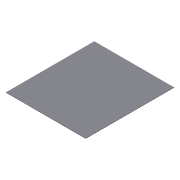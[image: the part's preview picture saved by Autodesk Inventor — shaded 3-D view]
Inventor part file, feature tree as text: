
AUTODESK INVENTOR PART (.ipt)
format: ipt  version: 2016 (Build 200138000, 138)  size: 68,608 bytes
history: native  units: mm
features: extrude x1, sketch x1
ambient origin geometry x8: Origin, YZ Plane, XZ Plane, XY Plane, X Axis, Y Axis, Z Axis, Center Point
bodies: Volumenkörper1 (feature_tree)
feature tree (2):
  extrude  "Extrusion1"  Depth=603.0mm
  sketch  "Skizze1"  dims[d0=700.0mm d1=603.0mm d2=3.0mm d3=0.0mm]
